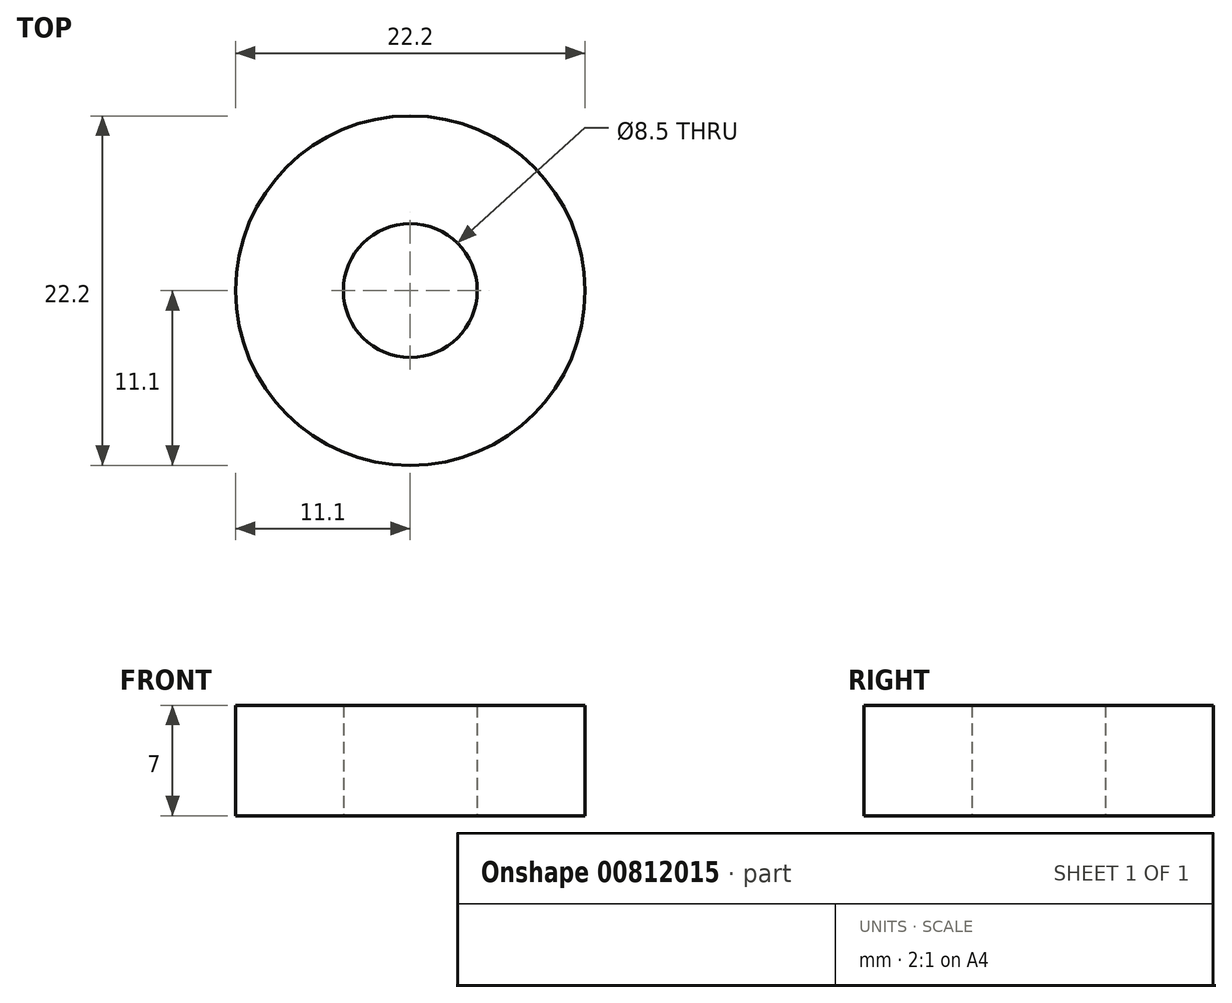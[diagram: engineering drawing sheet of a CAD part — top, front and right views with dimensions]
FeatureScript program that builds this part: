
annotation { "Feature Type Name" : "Feature", "Feature Type Description" : "" }
export const myFeature = defineFeature(function(context is Context, id is Id, definition is map)
    precondition{}
    {
        {
            var Q0;
            Q0=qCreatedBy(makeId("Top.planeOp"),FACE);
            var sketch = newSketch(context, id + "F0", { "sketchPlane" : qUnion([Q0])});
            skCircle(sketch, "E0", {"center": v(0, 0) * mm, "radius": 4.25 * mm});
            skCircle(sketch, "E1", {"center": v(0, 0) * mm, "radius": 11.1 * mm});
            skSolve(sketch);
        }
        {
            var Q0;
            Q0 = qSketchRegion(id + "F0", true);
            extrude(context, id + "F1", {"entities" : qUnion([Q0]), "depth" : 7 * mm, "offsetDistance" : 25 * mm});
        }
    });
